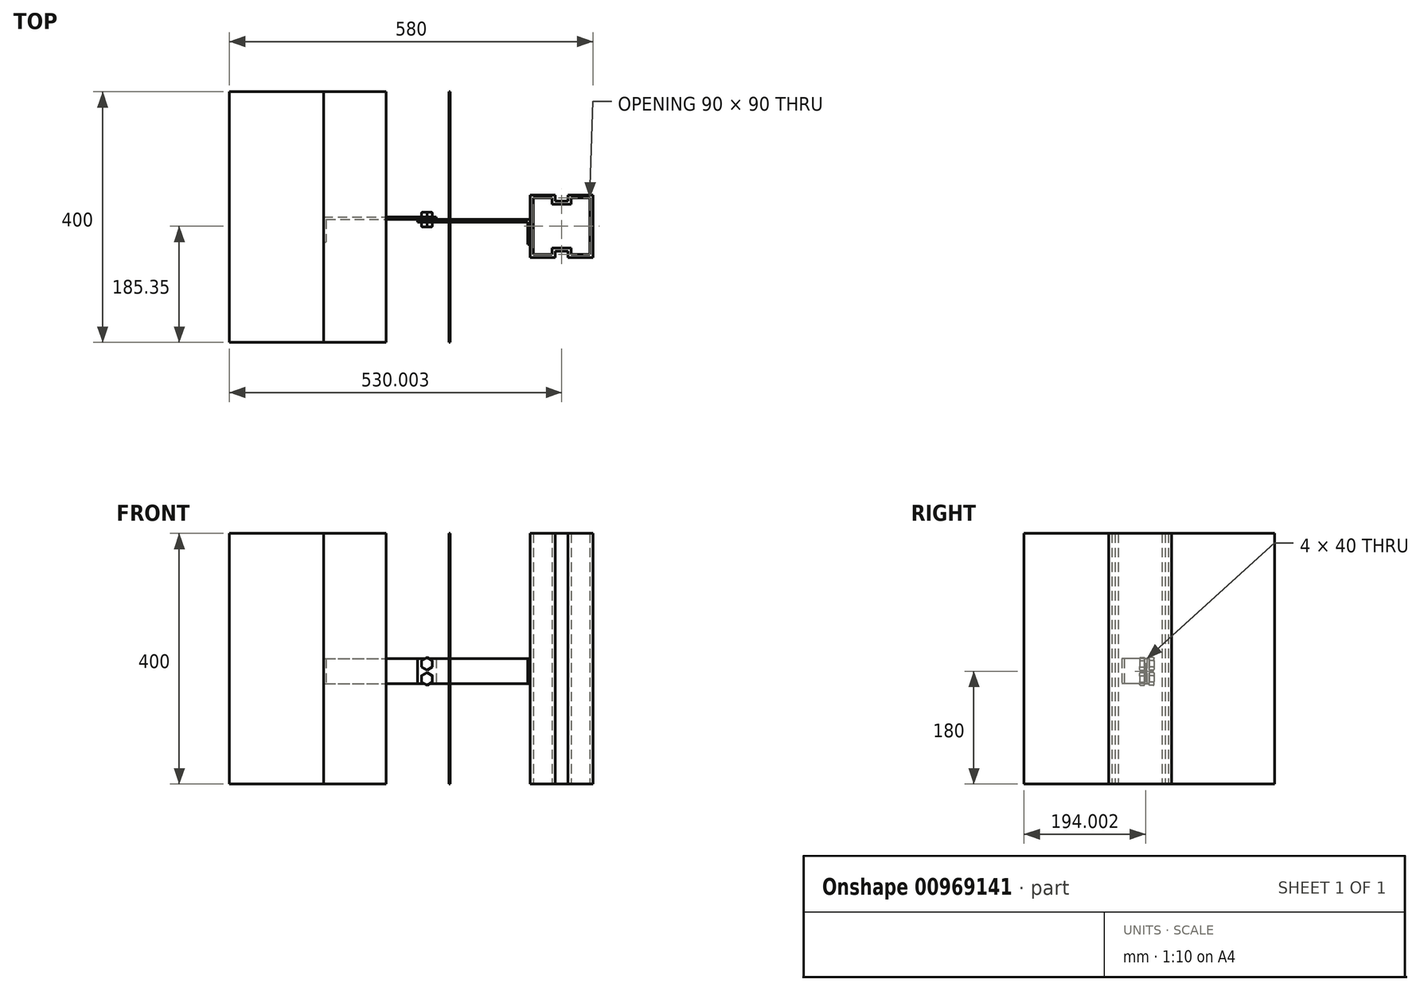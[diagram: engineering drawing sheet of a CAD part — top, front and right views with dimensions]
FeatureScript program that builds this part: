
annotation { "Feature Type Name" : "Feature", "Feature Type Description" : "" }
export const myFeature = defineFeature(function(context is Context, id is Id, definition is map)
    precondition{}
    {
        {
            var Q0;
            Q0=qCreatedBy(makeId("Top.planeOp"),FACE);
            var sketch = newSketch(context, id + "F0", { "sketchPlane" : qUnion([Q0])});
            skLineSegment(sketch, "E0", {"start": v(-54.77, 64.65) * mm, "end": v(125.23, 64.65) * mm});
            skLineSegment(sketch, "E1", {"start": v(-54.77, 64.65) * mm, "end": v(-54.77, 24.65) * mm});
            skLineSegment(sketch, "E2.0", {"start": v(-50.77, 60.65) * mm, "end": v(125.23, 60.65) * mm});
            skLineSegment(sketch, "E2.1", {"start": v(-50.77, 60.65) * mm, "end": v(-50.77, 24.65) * mm});
            skLineSegment(sketch, "E3", {"start": v(-54.77, 24.65) * mm, "end": v(-50.77, 24.65) * mm});
            skLineSegment(sketch, "E4", {"start": v(125.23, 60.65) * mm, "end": v(125.23, 64.65) * mm});
            skSolve(sketch);
        }
        {
            var Q0;
            Q0 = qSketchRegion(id + "F0", true);
            extrude(context, id + "F1", {"entities" : qUnion([Q0]), "depth" : 40 * mm, "offsetDistance" : 25 * mm});
        }
        {
            var Q0;
            Q0=qCreatedBy(makeId("Top.planeOp"),FACE);
            var sketch = newSketch(context, id + "F2", { "sketchPlane" : qUnion([Q0])});
            skLineSegment(sketch, "E5", {"start": v(95.23, 60.65) * mm, "end": v(275.23, 60.65) * mm});
            skLineSegment(sketch, "E6", {"start": v(275.23, 60.65) * mm, "end": v(275.23, 20.65) * mm});
            skLineSegment(sketch, "E7.0", {"start": v(271.23, 56.65) * mm, "end": v(271.23, 20.65) * mm});
            skLineSegment(sketch, "E7.1", {"start": v(95.23, 56.65) * mm, "end": v(271.23, 56.65) * mm});
            skLineSegment(sketch, "E8", {"start": v(95.23, 60.65) * mm, "end": v(95.23, 56.65) * mm});
            skLineSegment(sketch, "E9", {"start": v(271.23, 20.65) * mm, "end": v(275.23, 20.65) * mm});
            skSolve(sketch);
        }
        {
            var Q0;
            Q0 = qSketchRegion(id + "F2", true);
            extrude(context, id + "F3", {"entities" : qUnion([Q0]), "depth" : 40 * mm, "offsetDistance" : 25 * mm});
        }
        {
            var Q0;
            Q0=makeQuery(id+"F3.opExtrude","SWEPT_FACE",FACE,{"disambiguationData":[OSD([sQuery(id+"F2.wireOp",EDGE,"E7.1")])]});
            var sketch = newSketch(context, id + "F4", { "sketchPlane" : qUnion([Q0])});
            skLineSegment(sketch, "E10", {"start": v(110.23, 40) * mm, "end": v(110.23, 0) * mm, "construction": true});
            skLineSegment(sketch, "E11", {"start": v(95.23, 20) * mm, "end": v(142.25, 20) * mm, "construction": true});
            skPoint(sketch, "E11.endSnap0", {"position": v(110.23, 20) * mm});
            skCircle(sketch, "E12.cCircle", {"center": v(110.23, 32) * mm, "radius": 8.66 * mm, "construction": true});
            skLineSegment(sketch, "E12.0", {"start": v(118.9, 37) * mm, "end": v(118.9, 27) * mm});
            skLineSegment(sketch, "E12.1", {"start": v(118.9, 27) * mm, "end": v(110.23, 22) * mm});
            skLineSegment(sketch, "E12.2", {"start": v(110.23, 22) * mm, "end": v(101.57, 27) * mm});
            skLineSegment(sketch, "E12.3", {"start": v(101.57, 27) * mm, "end": v(101.57, 37) * mm});
            skLineSegment(sketch, "E12.4", {"start": v(101.57, 37) * mm, "end": v(110.23, 42) * mm});
            skLineSegment(sketch, "E12.5", {"start": v(110.23, 42) * mm, "end": v(118.9, 37) * mm});
            skPoint(sketch, "E12.0.midPoint", {"position": v(118.9, 32) * mm});
            skLineSegment(sketch, "E13.MirrorCS", {"start": v(101.57, 3) * mm, "end": v(110.23, -2) * mm});
            skPoint(sketch, "E14.MirrorP", {"position": v(118.9, 8) * mm});
            skLineSegment(sketch, "E15.MirrorCS", {"start": v(101.57, 13) * mm, "end": v(101.57, 3) * mm});
            skLineSegment(sketch, "E16.MirrorCS", {"start": v(118.9, 13) * mm, "end": v(110.23, 18) * mm});
            skLineSegment(sketch, "E17.MirrorCS", {"start": v(110.23, 18) * mm, "end": v(101.57, 13) * mm});
            skLineSegment(sketch, "E18.MirrorCS", {"start": v(118.9, 3) * mm, "end": v(118.9, 13) * mm});
            skCircle(sketch, "E19.MirrorC", {"center": v(110.23, 8) * mm, "radius": 8.66 * mm, "construction": true});
            skLineSegment(sketch, "E20.MirrorCS", {"start": v(110.23, -2) * mm, "end": v(118.9, 3) * mm});
            skSolve(sketch);
        }
        {
            var Q0;
            Q0 = qSketchRegion(id + "F4", true);
            extrude(context, id + "F5", {"entities" : qUnion([Q0]), "depth" : 7.5 * mm, "offsetDistance" : 25 * mm});
        }
        {
            var Q0;
            Q0=makeQuery(id+"F5.opExtrude","CAP_EDGE",EDGE,{"disambiguationData":[OSD([sQuery(id+"F4.wireOp",EDGE,"E12.4")])],"isStart":false});
            var Q1;
            Q1=makeQuery(id+"F5.opExtrude","CAP_EDGE",EDGE,{"disambiguationData":[OSD([sQuery(id+"F4.wireOp",EDGE,"E12.3")])],"isStart":false});
            var Q2;
            Q2=makeQuery(id+"F5.opExtrude","CAP_EDGE",EDGE,{"disambiguationData":[OSD([sQuery(id+"F4.wireOp",EDGE,"E12.2")])],"isStart":false});
            var Q3;
            Q3=makeQuery(id+"F5.opExtrude","CAP_EDGE",EDGE,{"disambiguationData":[OSD([sQuery(id+"F4.wireOp",EDGE,"E12.1")])],"isStart":false});
            var Q4;
            Q4=makeQuery(id+"F5.opExtrude","CAP_EDGE",EDGE,{"disambiguationData":[OSD([sQuery(id+"F4.wireOp",EDGE,"E12.0")])],"isStart":false});
            var Q5;
            Q5=makeQuery(id+"F5.opExtrude","CAP_EDGE",EDGE,{"disambiguationData":[OSD([sQuery(id+"F4.wireOp",EDGE,"E12.5")])],"isStart":false});
            var Q6;
            Q6=makeQuery(id+"F5.opExtrude","CAP_EDGE",EDGE,{"disambiguationData":[OSD([sQuery(id+"F4.wireOp",EDGE,"E17.MirrorCS")])],"isStart":false});
            var Q7;
            Q7=makeQuery(id+"F5.opExtrude","CAP_EDGE",EDGE,{"disambiguationData":[OSD([sQuery(id+"F4.wireOp",EDGE,"E15.MirrorCS")])],"isStart":false});
            var Q8;
            Q8=makeQuery(id+"F5.opExtrude","CAP_EDGE",EDGE,{"disambiguationData":[OSD([sQuery(id+"F4.wireOp",EDGE,"E16.MirrorCS")])],"isStart":false});
            var Q9;
            Q9=makeQuery(id+"F5.opExtrude","CAP_EDGE",EDGE,{"disambiguationData":[OSD([sQuery(id+"F4.wireOp",EDGE,"E18.MirrorCS")])],"isStart":false});
            var Q10;
            Q10=makeQuery(id+"F5.opExtrude","CAP_EDGE",EDGE,{"disambiguationData":[OSD([sQuery(id+"F4.wireOp",EDGE,"E20.MirrorCS")])],"isStart":false});
            var Q11;
            Q11=makeQuery(id+"F5.opExtrude","CAP_EDGE",EDGE,{"disambiguationData":[OSD([sQuery(id+"F4.wireOp",EDGE,"E13.MirrorCS")])],"isStart":false});
            fillet(context, id + "F6", {"entities" : qUnion([Q0, Q1, Q2, Q3, Q4, Q5, Q6, Q7, Q8, Q9, Q10, Q11]), "radius" : 1 * mm, "tangentPropagation" : true, "allowEdgeOverflow" : false});
        }
        {
            var Q0;
            Q0=makeQuery(id+"F5.opExtrude","SWEPT_BODY",BODY,{"disambiguationData":[OSD([sQuery(id+"F4.wireOp",EDGE,"E12.0"),sQuery(id+"F4.wireOp",EDGE,"E12.1"),sQuery(id+"F4.wireOp",EDGE,"E12.2"),sQuery(id+"F4.wireOp",EDGE,"E12.3"),sQuery(id+"F4.wireOp",EDGE,"E12.4"),sQuery(id+"F4.wireOp",EDGE,"E12.5")])]});
            var Q1;
            Q1=makeQuery(id+"F5.opExtrude","SWEPT_BODY",BODY,{"disambiguationData":[OSD([sQuery(id+"F4.wireOp",EDGE,"E15.MirrorCS"),sQuery(id+"F4.wireOp",EDGE,"E13.MirrorCS"),sQuery(id+"F4.wireOp",EDGE,"E16.MirrorCS"),sQuery(id+"F4.wireOp",EDGE,"E17.MirrorCS"),sQuery(id+"F4.wireOp",EDGE,"E18.MirrorCS"),sQuery(id+"F4.wireOp",EDGE,"E20.MirrorCS")])]});
            var Q2;
            Q2=makeQuery(id+"F3.opExtrude","SWEPT_FACE",FACE,{"disambiguationData":[OSD([sQuery(id+"F2.wireOp",EDGE,"E5")])]});
            mirror(context, id + "F7", {"entities" : qUnion([Q0, Q1]), "mirrorPlane" : qUnion([Q2])});
        }
        {
            var Q0;
            Q0=makeQuery(id+"F3.opExtrude","CAP_FACE",FACE,{"disambiguationData":[OSD([sQuery(id+"F2.wireOp",EDGE,"E5"),sQuery(id+"F2.wireOp",EDGE,"E6"),sQuery(id+"F2.wireOp",EDGE,"E7.0"),sQuery(id+"F2.wireOp",EDGE,"E7.1"),sQuery(id+"F2.wireOp",EDGE,"E8"),sQuery(id+"F2.wireOp",EDGE,"E9")])],"isStart":false});
            var sketch = newSketch(context, id + "F8", { "sketchPlane" : qUnion([Q0])});
            skLineSegment(sketch, "E21", {"start": v(275.23, 100) * mm, "end": v(315.23, 100) * mm});
            skLineSegment(sketch, "E22", {"start": v(315.23, 100) * mm, "end": v(315.23, 90) * mm});
            skLineSegment(sketch, "E23", {"start": v(315.23, 90) * mm, "end": v(335.23, 90) * mm});
            skLineSegment(sketch, "E24", {"start": v(335.23, 90) * mm, "end": v(335.23, 100) * mm});
            skLineSegment(sketch, "E25", {"start": v(335.23, 100) * mm, "end": v(375.23, 100) * mm});
            skLineSegment(sketch, "E26", {"start": v(375.23, 0) * mm, "end": v(375.23, 100) * mm});
            skLineSegment(sketch, "E27", {"start": v(275.23, 100) * mm, "end": v(275.23, 0) * mm});
            skLineSegment(sketch, "E28", {"start": v(375.23, 50) * mm, "end": v(275.23, 50) * mm, "construction": true});
            skLineSegment(sketch, "E29", {"start": v(325.23, 100) * mm, "end": v(325.23, 0) * mm, "construction": true});
            skLineSegment(sketch, "E30.MirrorCS", {"start": v(315.23, 10) * mm, "end": v(335.23, 10) * mm});
            skLineSegment(sketch, "E31.MirrorCS", {"start": v(315.23, 0) * mm, "end": v(315.23, 10) * mm});
            skLineSegment(sketch, "E32.MirrorCS", {"start": v(335.23, 10) * mm, "end": v(335.23, 0) * mm});
            skLineSegment(sketch, "E33.MirrorCS", {"start": v(275.23, 0) * mm, "end": v(315.23, 0) * mm});
            skLineSegment(sketch, "E34.MirrorCS", {"start": v(335.23, 0) * mm, "end": v(375.23, 0) * mm});
            skLineSegment(sketch, "E35.0", {"start": v(280.23, 95) * mm, "end": v(280.23, 5) * mm});
            skLineSegment(sketch, "E35.1", {"start": v(340.23, 95) * mm, "end": v(370.23, 95) * mm});
            skLineSegment(sketch, "E35.2", {"start": v(340.23, 85) * mm, "end": v(340.23, 95) * mm});
            skLineSegment(sketch, "E35.3", {"start": v(310.23, 85) * mm, "end": v(340.23, 85) * mm});
            skLineSegment(sketch, "E35.4", {"start": v(310.23, 95) * mm, "end": v(310.23, 85) * mm});
            skLineSegment(sketch, "E35.5", {"start": v(370.23, 5) * mm, "end": v(370.23, 95) * mm});
            skLineSegment(sketch, "E35.6", {"start": v(280.23, 95) * mm, "end": v(310.23, 95) * mm});
            skLineSegment(sketch, "E35.7", {"start": v(340.23, 5) * mm, "end": v(370.23, 5) * mm});
            skLineSegment(sketch, "E35.8", {"start": v(340.23, 15) * mm, "end": v(340.23, 5) * mm});
            skLineSegment(sketch, "E35.9", {"start": v(310.23, 15) * mm, "end": v(340.23, 15) * mm});
            skLineSegment(sketch, "E35.10", {"start": v(310.23, 5) * mm, "end": v(310.23, 15) * mm});
            skLineSegment(sketch, "E35.11", {"start": v(280.23, 5) * mm, "end": v(310.23, 5) * mm});
            skSolve(sketch);
        }
        {
            var Q0;
            Q0 = qSketchRegion(id + "F8", true);
            extrude(context, id + "F9", {"entities" : qUnion([Q0]), "depth" : 200 * mm, "offsetDistance" : 25 * mm, "hasSecondDirection" : true, "secondDirectionOppositeDirection" : true, "secondDirectionDepth" : 200 * mm});
        }
        {
            var Q0;
            Q0=makeQuery(id+"F1.opExtrude","CAP_FACE",FACE,{"disambiguationData":[OSD([sQuery(id+"F0.wireOp",EDGE,"E0"),sQuery(id+"F0.wireOp",EDGE,"E1"),sQuery(id+"F0.wireOp",EDGE,"E2.0"),sQuery(id+"F0.wireOp",EDGE,"E2.1"),sQuery(id+"F0.wireOp",EDGE,"E3"),sQuery(id+"F0.wireOp",EDGE,"E4")])],"isStart":false});
            var sketch = newSketch(context, id + "F10", { "sketchPlane" : qUnion([Q0])});
            skLineSegment(sketch, "E36.bottom", {"start": v(-54.77, 264.65) * mm, "end": v(-204.77, 264.65) * mm});
            skLineSegment(sketch, "E36.top", {"start": v(-54.77, -135.35) * mm, "end": v(-204.77, -135.35) * mm});
            skLineSegment(sketch, "E36.left", {"start": v(-54.77, 264.65) * mm, "end": v(-54.77, -135.35) * mm});
            skLineSegment(sketch, "E36.right", {"start": v(-204.77, 264.65) * mm, "end": v(-204.77, -135.35) * mm});
            skSolve(sketch);
        }
        {
            var Q0;
            Q0 = qSketchRegion(id + "F10", true);
            extrude(context, id + "F11", {"entities" : qUnion([Q0]), "depth" : 200 * mm, "offsetDistance" : 25 * mm, "hasSecondDirection" : true, "secondDirectionOppositeDirection" : true, "secondDirectionDepth" : 200 * mm});
        }
        {
            var Q0;
            Q0=makeQuery(id+"F11.opExtrude","SWEPT_FACE",FACE,{"disambiguationData":[OSD([sQuery(id+"F10.wireOp",EDGE,"E36.left")])]});
            var sketch = newSketch(context, id + "F12", { "sketchPlane" : qUnion([Q0])});
            skLineSegment(sketch, "E37.0", {"start": v(264.65, 240) * mm, "end": v(-135.35, 240) * mm});
            skLineSegment(sketch, "E37.1", {"start": v(-135.35, 240) * mm, "end": v(-135.35, -160) * mm});
            skLineSegment(sketch, "E37.2", {"start": v(264.65, 240) * mm, "end": v(264.65, -160) * mm});
            skLineSegment(sketch, "E37.3", {"start": v(264.65, -160) * mm, "end": v(-135.35, -160) * mm});
            skSolve(sketch);
        }
        {
            var Q0;
            Q0 = qSketchRegion(id + "F12", true);
            extrude(context, id + "F13", {"entities" : qUnion([Q0]), "depth" : 100 * mm, "offsetDistance" : 25 * mm});
        }
        {
            var Q0;
            Q0=makeQuery(id+"F13.opExtrude","CAP_FACE",FACE,{"disambiguationData":[OSD([sQuery(id+"F12.wireOp",EDGE,"E37.0"),sQuery(id+"F12.wireOp",EDGE,"E37.1"),sQuery(id+"F12.wireOp",EDGE,"E37.2"),sQuery(id+"F12.wireOp",EDGE,"E37.3")])],"isStart":false});
            var sketch = newSketch(context, id + "F14", { "sketchPlane" : qUnion([Q0])});
            skLineSegment(sketch, "E38.0", {"start": v(264.65, 240) * mm, "end": v(-135.35, 240) * mm});
            skLineSegment(sketch, "E38.1", {"start": v(-135.35, 240) * mm, "end": v(-135.35, -160) * mm});
            skLineSegment(sketch, "E38.2", {"start": v(264.65, 240) * mm, "end": v(264.65, -160) * mm});
            skLineSegment(sketch, "E38.3", {"start": v(264.65, -160) * mm, "end": v(-135.35, -160) * mm});
            skSolve(sketch);
        }
        {
            var Q0;
            Q0=makeQuery(id+"F14.imprint","IMPRINT",FACE,{"disambiguationData":[TD([[makeQuery(id+"F14.imprint","IMPRINT",EDGE,{"derivedFrom":sQuery(id+"F14.wireOp",EDGE,"E38.0")}),1.0]])]});
            cPlane(context, id + "F15", {"entities" : qUnion([Q0]), "cplaneType" : CPlaneType.OFFSET, "offset" : 100 * mm, "width" : 150 * mm, "height" : 150 * mm});
        }
        {
            var Q0;
            Q0=qCreatedBy(id+"F15.planeOp",FACE);
            var sketch = newSketch(context, id + "F16", { "sketchPlane" : qUnion([Q0])});
            skLineSegment(sketch, "E39.0", {"start": v(264.65, 240) * mm, "end": v(-135.35, 240) * mm});
            skLineSegment(sketch, "E39.1", {"start": v(-135.35, 240) * mm, "end": v(-135.35, -160) * mm});
            skLineSegment(sketch, "E39.2", {"start": v(264.65, 240) * mm, "end": v(264.65, -160) * mm});
            skLineSegment(sketch, "E39.3", {"start": v(264.65, -160) * mm, "end": v(-135.35, -160) * mm});
            skSolve(sketch);
        }
        {
            var Q0;
            Q0 = qSketchRegion(id + "F16", true);
            extrude(context, id + "F17", {"entities" : qUnion([Q0]), "operationType" : NewBodyOperationType.ADD, "depth" : 2 * mm, "offsetDistance" : 25 * mm});
        }
    });
